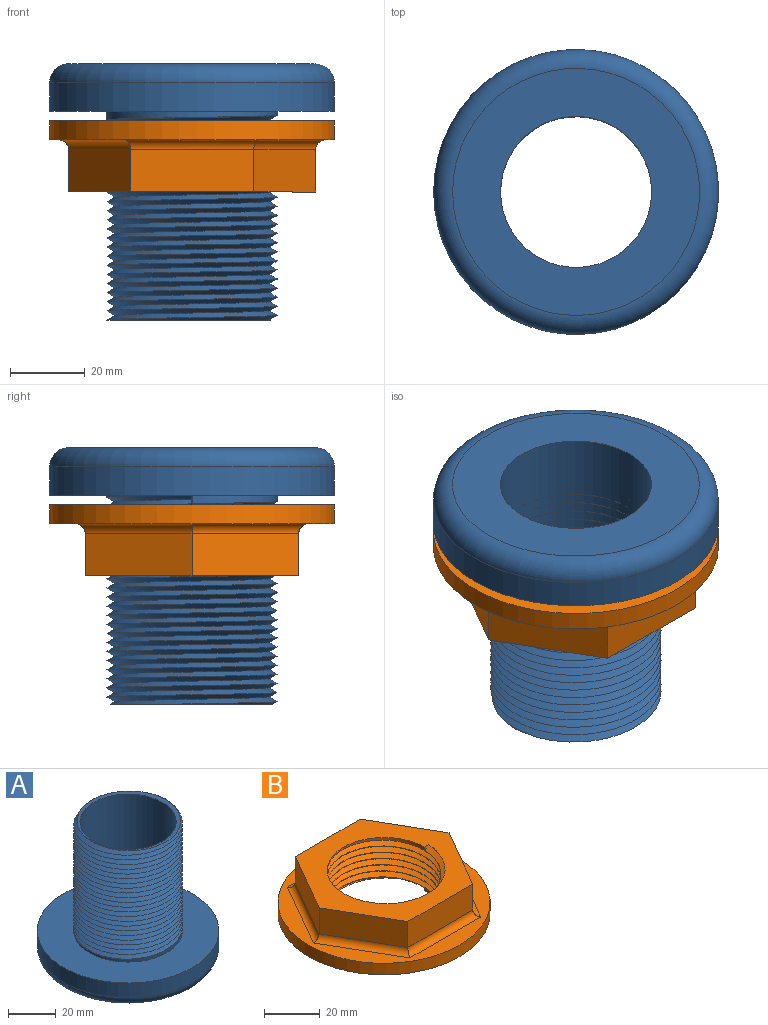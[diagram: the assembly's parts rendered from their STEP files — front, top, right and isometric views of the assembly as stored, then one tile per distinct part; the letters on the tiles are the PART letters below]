
ASSEMBLY  parts=2 mates=1
PART A: 15 faces, bbox 84.5x84.5x72.1 mm
  f0: cylinder r=22.86mm len=3.22mm, axis (0,0,-1), area 0.1mm2, adj f1,f7,f10
  f1: plane 45.77x45.51mm, normal (0,0,1), area 202.3mm2, adj f0,f2,f7,f10,f11,f12
  f2: cylinder r=20.19mm len=68.58mm, axis (0,0,-1), area 8701.2mm2, adj f1,f4
  f3: cylinder r=22.86mm len=45.72mm, axis (0,0,-1), area 151.9mm2, adj f6,f8,f13
  f4: plane 66.04x66.04mm, normal (0,0,-1), area 2144.3mm2, adj f2,f14
  f5: cylinder r=38.1mm len=76.2mm, axis (0,0,-1), area 1824.1mm2, adj f6,f14
  f6: plane 76.2x76.2mm, normal (0,0,1), area 2918.6mm2, adj f3,f5,f9
  f7: plane 0.28x0.11mm, normal (0,-1,0), area 0mm2, adj f0,f1,f10,f12
  f8: plane 2.48x2.2mm, normal (0,1,0), area 2.8mm2, adj f3,f9,f11,f12,f13
  f9: cylinder r=22.86mm len=9.39mm, axis (0,0,-1), area 0.8mm2, adj f6,f8,f13
  f10: bspline ~19.8x11.48mm, area 0.5mm2, adj f0,f1,f7,f11
  f11: bspline ~56.29x52.57mm, area 7395.1mm2, adj f1,f8,f10,f12
  f12: bspline ~57.09x52.57mm, area 7546.3mm2, adj f1,f7,f8,f11,f13
  f13: bspline ~52.79x45.72mm, area 15.8mm2, adj f3,f8,f9,f12
  f14: torus R=33.02mm, axis (0,0,1), area 1817.7mm2, adj f4,f5
PART B: 21 faces, bbox 76.3x76.3x21.7 mm
  f0: cylinder r=20.45mm len=40.89mm, axis (0,0,-1), area 415mm2, adj f1,f8,f11,f12,f13,f14
  f1: plane 76.27x76.27mm, normal (0,0,-1), area 3169mm2, adj f0,f9,f11,f12,f13
  f2: plane 33x11.43mm, normal (0,1,0), area 377.1mm2, adj f3,f7,f8,f15
  f3: plane 28.58x16.5mm, normal (-0.87,0.5,0), area 377.1mm2, adj f2,f4,f8,f17
  f4: plane 28.58x16.5mm, normal (-0.87,-0.5,0), area 377.1mm2, adj f3,f5,f8,f19
  f5: plane 33x11.43mm, normal (0,-1,0), area 377.1mm2, adj f4,f6,f8,f20
  f6: plane 28.58x16.5mm, normal (0.87,-0.5,0), area 377.1mm2, adj f5,f7,f8,f18
  f7: plane 28.58x16.5mm, normal (0.87,0.5,0), area 377.1mm2, adj f2,f6,f8,f16
  f8: plane 65.99x57.15mm, normal (0,0,1), area 1456.3mm2, adj f0,f2,f3,f4,f5,f6,f7,f13
  f9: cylinder r=38.1mm len=76.2mm, axis (0,0,-1), area 1216.1mm2, adj f1,f10
  f10: plane 76.2x76.2mm, normal (0,0,1), area 1206.6mm2, adj f9,f15,f16,f17,f18,f19,f20
  f11: plane 2.04x1.18mm, normal (0,1,0), area 1.2mm2, adj f0,f1,f13
  f12: bspline ~52.3x45.29mm, area 2329.9mm2, adj f0,f1,f13,f14
  f13: bspline ~52.3x45.29mm, area 2351.9mm2, adj f0,f1,f8,f11,f12,f14
  f14: plane 2.2x1.36mm, normal (0,-1,0), area 1.6mm2, adj f0,f8,f12,f13
  f15: cylinder r=2.54mm len=35.93mm, axis (-1,0,0), area 135.9mm2, adj f2,f10,f16,f17
  f16: cylinder r=2.54mm len=32.39mm, axis (-0.5,0.87,0), area 135.9mm2, adj f7,f10,f15,f18
  f17: cylinder r=2.54mm len=32.39mm, axis (-0.5,-0.87,0), area 135.9mm2, adj f3,f10,f15,f19
  f18: cylinder r=2.54mm len=32.39mm, axis (0.5,0.87,0), area 135.9mm2, adj f6,f10,f16,f20
  f19: cylinder r=2.54mm len=32.39mm, axis (0.5,-0.87,0), area 135.9mm2, adj f4,f10,f17,f20
  f20: cylinder r=2.54mm len=35.93mm, axis (1,0,0), area 135.9mm2, adj f5,f10,f18,f19
PLACE A rot(axis=(0,1,0),180deg) t=(-163.52,-106.81,59.44)mm fixed
PLACE B rot(axis=(0,-1,0),180deg) t=(-163.52,-106.81,44.2)mm
MATE cylindrical B.f9 <-> A.f5  axis (0,0,-1) through (-163.52,-106.81,39.12)mm
